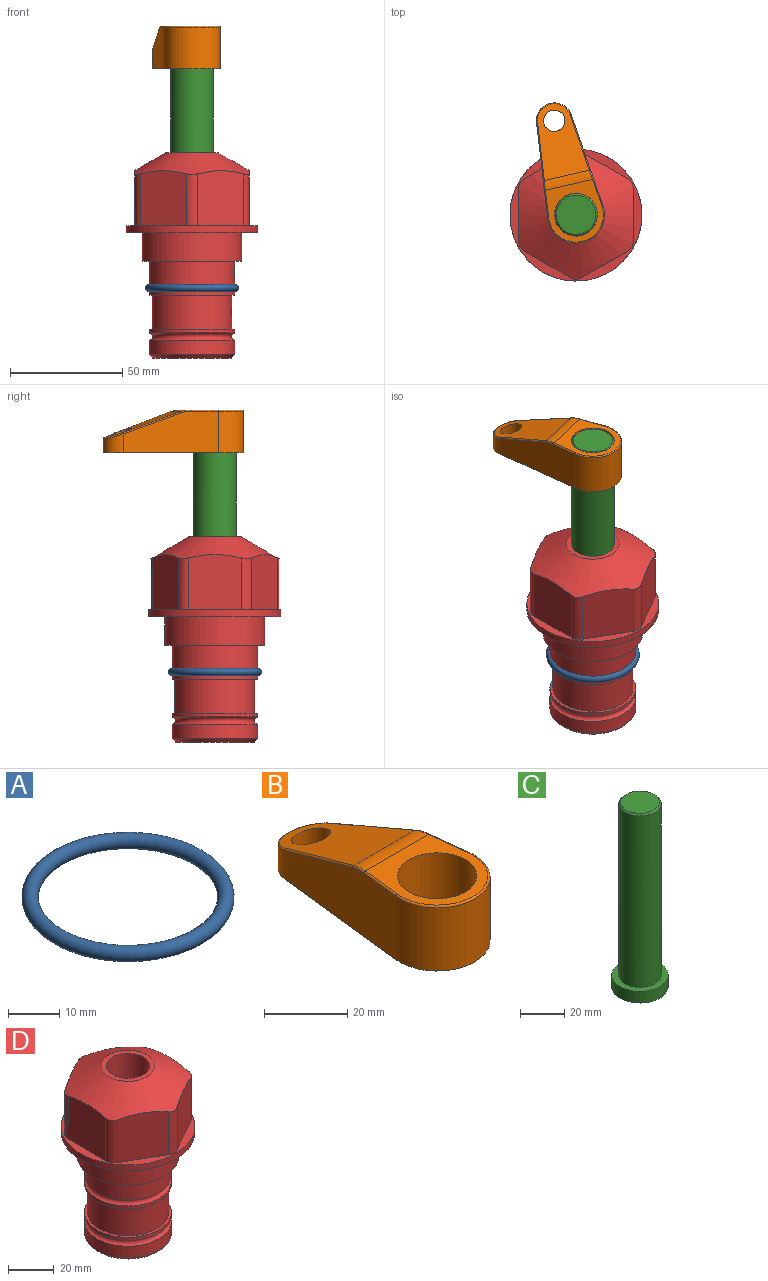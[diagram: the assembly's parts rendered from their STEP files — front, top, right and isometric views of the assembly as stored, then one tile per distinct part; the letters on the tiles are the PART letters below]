
ASSEMBLY  parts=4 mates=2
PART A: 1 faces, bbox 44.7x44.7x3.2 mm
  f0: torus R=19.05mm, axis (0,0,1), area 1193.9mm2
PART B: 44 faces, bbox 27.5x64.5x19.1 mm
  f0: plane 2.3x0.95mm, normal (0,0,-1), area 1mm2, adj f25,f30,f34
  f1: plane 63.5x25.4mm, normal (0,0,-1), area 561.7mm2, adj f2,f3,f4,f5,f6,f7,f19,f20
  f2: cylinder r=12.7mm len=25.4mm, axis (0,0,-1), area 792.2mm2, adj f1,f3,f5,f13
  f3: plane 42.33x18.54mm, normal (0.99,0.11,0), area 647mm2, adj f1,f2,f4,f11,f12,f14
  f4: cylinder r=7.94mm len=15.78mm, axis (0,0,-1), area 158.6mm2, adj f1,f3,f5,f16
  f5: plane 42.33x18.54mm, normal (-0.99,0.11,0), area 647mm2, adj f1,f2,f4,f15,f17,f18
  f6: cylinder r=9.53mm len=19.05mm, axis (0,0,-1), area 1140.1mm2, adj f1,f8
  f7: cylinder r=4.76mm len=10.98mm, axis (0,0,-1), area 276.1mm2, adj f1,f9
  f8: plane 25.83x24.38mm, normal (0,0,1), area 262.2mm2, adj f6,f10,f11,f13,f15
  f9: plane 32.49x20.55mm, normal (0,0.34,0.94), area 489.9mm2, adj f7,f10,f14,f16,f18
  f10: cylinder r=12.7mm len=21.49mm, axis (-1,0,0), area 93.2mm2, adj f8,f9,f12,f17
  f11: cylinder r=0.51mm len=12.34mm, axis (0.11,-0.99,0), area 9.9mm2, adj f3,f8,f12,f13
  f12: bspline ~7.62x1.64mm, area 3.5mm2, adj f3,f10,f11,f14
  f13: torus R=12.19mm, axis (0,0,1), area 33.6mm2, adj f2,f8,f11,f15
  f14: cylinder r=0.51mm len=26.01mm, axis (0.1,-0.93,0.34), area 21.6mm2, adj f3,f9,f12,f16
  f15: cylinder r=0.51mm len=12.34mm, axis (0.11,0.99,0), area 9.9mm2, adj f5,f8,f13,f17
  f16: bspline ~15.78x7.05mm, area 15.7mm2, adj f4,f9,f14,f18
  f17: bspline ~7.62x1.64mm, area 3.5mm2, adj f5,f10,f15,f18
  f18: cylinder r=0.51mm len=26.01mm, axis (0.1,0.93,-0.34), area 21.6mm2, adj f5,f9,f16,f17
  f19: plane 21.6x14.29mm, normal (-0.99,-0.11,0), area 242.6mm2, adj f1,f26,f28,f34,f36,f38
  f20: plane 21.6x14.29mm, normal (0.99,-0.11,0), area 242.6mm2, adj f1,f27,f29,f37,f39,f41
  f21: cylinder r=12.7mm len=14.29mm, axis (0,0,-1), area 173.2mm2, adj f1,f26,f27,f30,f31,f33
  f22: cylinder r=7.94mm len=7.63mm, axis (0,0,-1), area 53.8mm2, adj f1,f28,f29,f42
  f23: plane 2.3x0.95mm, normal (0,0,-1), area 1mm2, adj f25,f33,f37
  f24: plane 17.94x12.32mm, normal (0,-0.34,-0.94), area 191.2mm2, adj f25,f38,f41,f42
  f25: cylinder r=9.53mm len=12.93mm, axis (-1,0,0), area 37.5mm2, adj f0,f23,f24,f31,f36,f39
  f26: cylinder r=1.59mm len=14.29mm, axis (0,0,-1), area 49mm2, adj f1,f19,f21,f32
  f27: cylinder r=1.59mm len=14.29mm, axis (0,0,-1), area 49mm2, adj f1,f20,f21,f35
  f28: cylinder r=1.59mm len=7.28mm, axis (0,0,-1), area 22.1mm2, adj f1,f19,f22,f40
  f29: cylinder r=1.59mm len=7.28mm, axis (0,0,-1), area 22.1mm2, adj f1,f20,f22,f43
  f30: torus R=14.29mm, axis (0,0,1), area 5.8mm2, adj f0,f21,f31,f32
  f31: bspline ~11.06x2.73mm, area 20.8mm2, adj f21,f25,f30,f33
  f32: sphere r=1.59mm, area 5.4mm2, adj f26,f30,f34
  f33: torus R=14.29mm, axis (0,0,1), area 5.8mm2, adj f21,f23,f31,f35
  f34: cylinder r=1.59mm len=1.68mm, axis (-0.11,0.99,0), area 2.4mm2, adj f0,f19,f32,f36
  f35: sphere r=1.59mm, area 5.4mm2, adj f27,f33,f37
  f36: bspline ~5.82x2.33mm, area 7.7mm2, adj f19,f25,f34,f38
  f37: cylinder r=1.59mm len=1.68mm, axis (0.11,0.99,0), area 2.4mm2, adj f20,f23,f35,f39
  f38: cylinder r=1.59mm len=18.33mm, axis (0.1,-0.93,0.34), area 46.7mm2, adj f19,f24,f36,f40
  f39: bspline ~5.82x2.33mm, area 7.7mm2, adj f20,f25,f37,f41
  f40: sphere r=1.59mm, area 3.6mm2, adj f28,f38,f42
  f41: cylinder r=1.59mm len=18.33mm, axis (0.1,0.93,-0.34), area 46.7mm2, adj f20,f24,f39,f43
  f42: bspline ~8.31x1.84mm, area 15.3mm2, adj f22,f24,f40,f43
  f43: sphere r=1.59mm, area 3.6mm2, adj f29,f41,f42
PART C: 6 faces, bbox 25.4x25.4x101.6 mm
  f0: plane 17.46x17.46mm, normal (0,0,1), area 239.5mm2, adj f5
  f1: plane 25.4x25.4mm, normal (0,0,-1), area 506.7mm2, adj f2
  f2: cylinder r=12.7mm len=25.4mm, axis (0,0,1), area 506.7mm2, adj f1,f3
  f3: plane 25.4x25.4mm, normal (0,0,1), area 221.7mm2, adj f2,f4
  f4: cylinder r=9.53mm len=94.46mm, axis (0,0,1), area 5653mm2, adj f3,f5
  f5: cone r=8.73mm half-angle=45deg, axis (0,0,-1), area 64.4mm2, adj f0,f4
PART D: 36 faces, bbox 58.7x58.7x91.2 mm
  f0: cylinder r=17.78mm len=35.56mm, axis (0,0,1), area 1670.8mm2, adj f23,f24,f31
  f1: cylinder r=19.05mm len=38.1mm, axis (0,0,1), area 1191.9mm2, adj f26,f27,f30
  f2: plane 58.66x58.66mm, normal (0,0,-1), area 1150.6mm2, adj f3,f28
  f3: cylinder r=29.33mm len=58.66mm, axis (0,0,-1), area 585.1mm2, adj f2,f4
  f4: plane 58.66x58.66mm, normal (0,0,1), area 475.9mm2, adj f3,f5,f6,f7,f8,f9,f10,f11
  f5: plane 24.5x20.32mm, normal (-0.5,0.87,0), area 562.8mm2, adj f4,f15,f16,f17
  f6: plane 24.5x20.32mm, normal (0.5,0.87,0), area 562.8mm2, adj f4,f14,f15,f17
  f7: plane 24.5x23.48mm, normal (1,0,0), area 562.8mm2, adj f4,f13,f14,f17
  f8: plane 24.5x20.32mm, normal (0.5,-0.87,0), area 562.8mm2, adj f4,f12,f13,f17
  f9: plane 24.5x20.32mm, normal (-0.5,-0.87,0), area 562.8mm2, adj f4,f11,f12,f17
  f10: plane 24.5x23.48mm, normal (-1,0,0), area 562.8mm2, adj f4,f11,f16,f17
  f11: cylinder r=5.08mm len=23.01mm, axis (0,0,-1), area 121.2mm2, adj f4,f9,f10,f17
  f12: cylinder r=5.08mm len=23.01mm, axis (0,0,-1), area 121.2mm2, adj f4,f8,f9,f17
  f13: cylinder r=5.08mm len=23.01mm, axis (0,0,-1), area 121.2mm2, adj f4,f7,f8,f17
  f14: cylinder r=5.08mm len=23.01mm, axis (0,0,-1), area 121.2mm2, adj f4,f6,f7,f17
  f15: cylinder r=5.08mm len=23.01mm, axis (0,0,-1), area 121.2mm2, adj f4,f5,f6,f17
  f16: cylinder r=5.08mm len=23.01mm, axis (0,0,-1), area 121.2mm2, adj f4,f5,f10,f17
  f17: cone r=11.73mm half-angle=60deg, axis (0,0,-1), area 2071.8mm2, adj f5,f6,f7,f8,f9,f10,f11,f12
  f18: plane 23.46x23.46mm, normal (0,0,1), area 147.4mm2, adj f17,f35
  f19: plane 34.93x34.93mm, normal (0,0,-1), area 958mm2, adj f29
  f20: cylinder r=19.05mm len=38.1mm, axis (0,0,1), area 760.1mm2, adj f21,f29
  f21: torus R=19.05mm, axis (0,0,1), area 565.3mm2, adj f20,f22
  f22: cylinder r=19.05mm len=38.1mm, axis (0,0,1), area 190mm2, adj f21,f23
  f23: plane 38.1x38.1mm, normal (0,0,1), area 146.9mm2, adj f0,f22
  f24: plane 38.1x38.1mm, normal (0,0,-1), area 146.9mm2, adj f0,f25
  f25: cylinder r=19.05mm len=38.1mm, axis (0,0,1), area 190mm2, adj f24,f26
  f26: torus R=19.05mm, axis (0,0,1), area 565.3mm2, adj f1,f25
  f27: plane 44.45x44.45mm, normal (0,0,-1), area 411.7mm2, adj f1,f28
  f28: cylinder r=22.23mm len=44.45mm, axis (0,0,1), area 1773.5mm2, adj f2,f27
  f29: cone r=19.05mm half-angle=45deg, axis (0,0,1), area 257.5mm2, adj f19,f20
  f30: cylinder r=3.17mm len=6.75mm, axis (-1,0,0), area 128mm2, adj f1,f33
  f31: cylinder r=3.17mm len=6.35mm, axis (-1,0,0), area 102.5mm2, adj f0,f33
  f32: plane 25.4x25.4mm, normal (0,0,1), area 506.7mm2, adj f33
  f33: cylinder r=12.7mm len=66.42mm, axis (0,0,-1), area 5236.2mm2, adj f30,f31,f32,f34
  f34: cone r=9.53mm half-angle=30deg, axis (0,0,-1), area 443.4mm2, adj f33,f35
  f35: cylinder r=9.53mm len=19.05mm, axis (0,0,-1), area 849mm2, adj f18,f34
PLACE A at identity
PLACE B rot(axis=(0,0,1),13deg) t=(0,0,72.9)mm
PLACE C rot(axis=(0,0,1),13deg) t=(0,0,18.29)mm
PLACE D at identity fixed
MATE cylindrical C.f2 <-> D.f0  axis (0,0,1) through (0,0,43.93)mm
MATE fastened B.f2 <-> C.f2  axis (0,0,-1) through (0,0,91.95)mm
